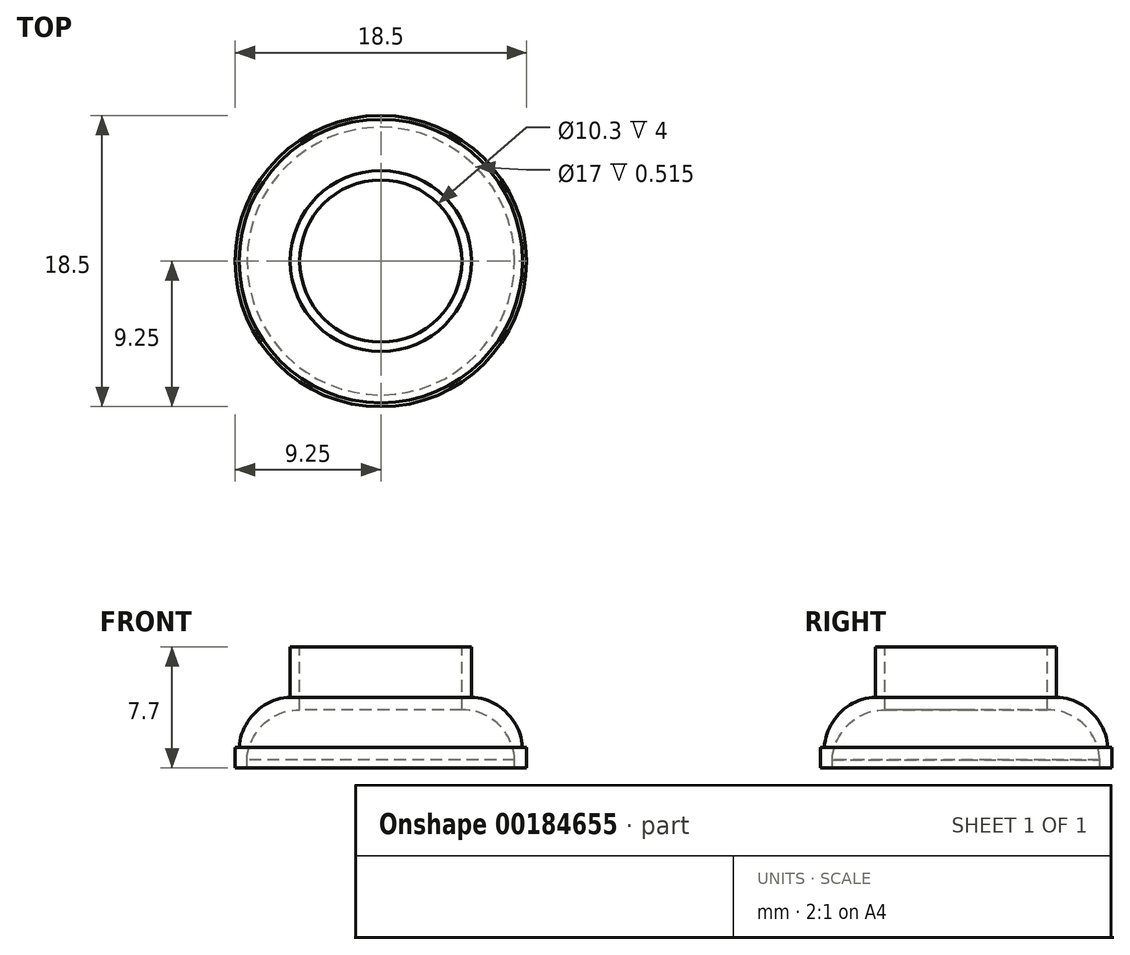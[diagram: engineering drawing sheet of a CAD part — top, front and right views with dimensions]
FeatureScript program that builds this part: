
annotation { "Feature Type Name" : "Feature", "Feature Type Description" : "" }
export const myFeature = defineFeature(function(context is Context, id is Id, definition is map)
    precondition{}
    {
        {
            var Q0;
            Q0=qCreatedBy(makeId("Front.planeOp"),FACE);
            var sketch = newSketch(context, id + "F0", { "sketchPlane" : qUnion([Q0])});
            skLineSegment(sketch, "E0", {"start": v(-5.75, 7.7) * mm, "end": v(-5.15, 7.7) * mm});
            skLineSegment(sketch, "E1", {"start": v(-5.15, 7.7) * mm, "end": v(-5.15, 3.7) * mm});
            skLineSegment(sketch, "E2", {"start": v(-5.75, 7.7) * mm, "end": v(-5.75, 4.5) * mm});
            skLineSegment(sketch, "E3", {"start": v(-8.5, 0) * mm, "end": v(-9.25, 0) * mm});
            skLineSegment(sketch, "E4", {"start": v(-9.25, 0) * mm, "end": v(-9.25, 1.31) * mm});
            skLineSegment(sketch, "E5", {"start": v(-9.25, 1.31) * mm, "end": v(-9, 1.31) * mm});
            skLineSegment(sketch, "E6", {"start": v(-8.5, 0) * mm, "end": v(-8.5, 0.52) * mm});
            skArc(sketch, "E7", {"start": v(-5.15, 3.7) * mm, "mid": v(-7.46, 2.78) * mm, "end": v(-8.5, 0.52) * mm});
            skArc(sketch, "E8", {"start": v(-5.75, 4.5) * mm, "mid": v(-7.98, 3.53) * mm, "end": v(-9, 1.31) * mm});
            skLineSegment(sketch, "E9", {"start": v(0, 6.6) * mm, "end": v(0, 3.24) * mm, "construction": true});
            skSolve(sketch);
        }
        {
            var Q0;
            Q0=qSketchRegion(id+"F0",true);
            var Q1;
            Q1=sQuery(id+"F0.wireOp",EDGE,"E9");
            revolve(context, id + "F1", {"entities" : qUnion([Q0]), "axis" : qUnion([Q1]), "revolveType" : RevolveType.FULL});
        }
    });
